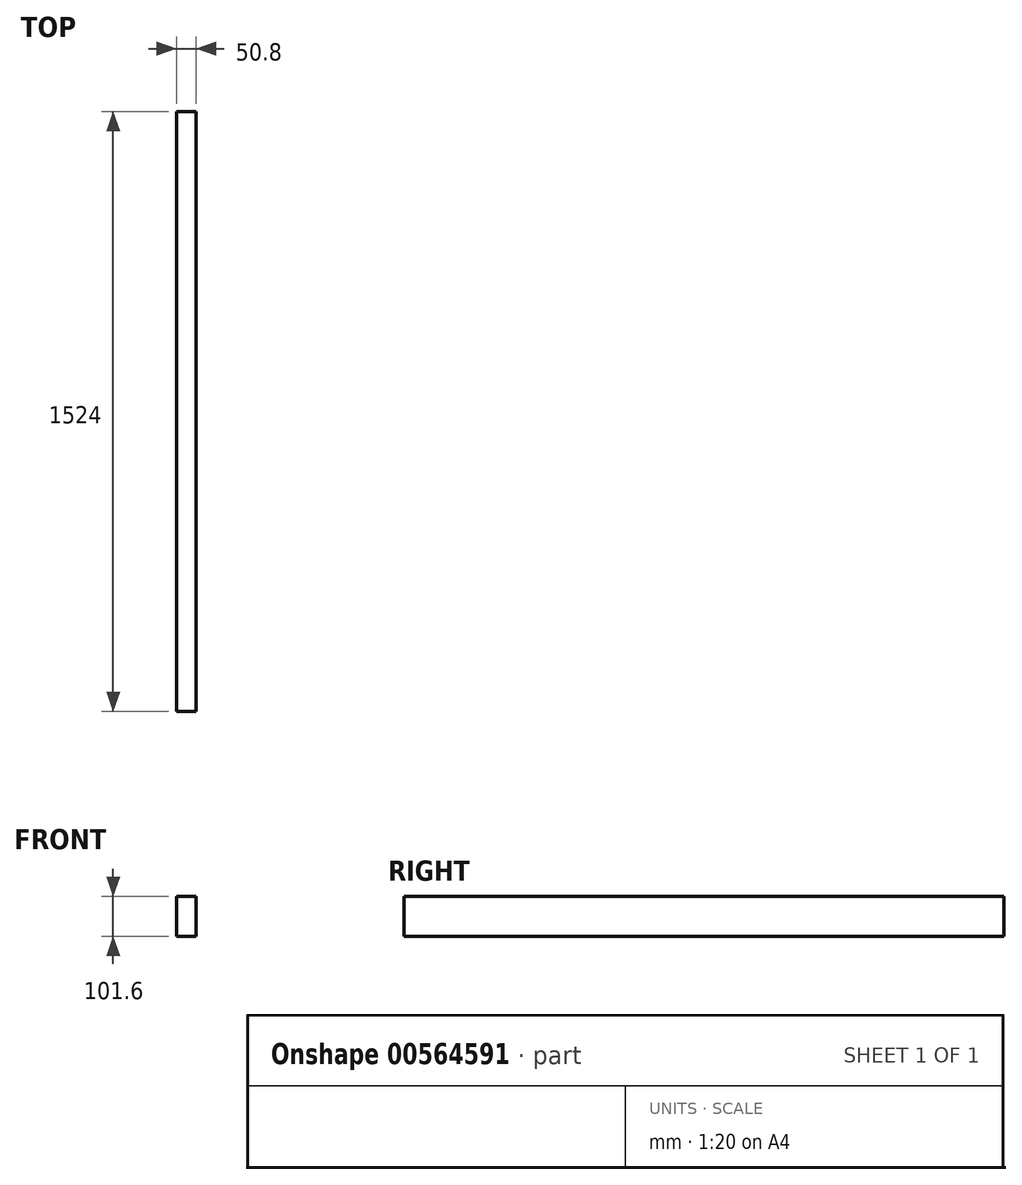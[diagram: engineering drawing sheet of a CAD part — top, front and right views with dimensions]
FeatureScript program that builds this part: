
annotation { "Feature Type Name" : "Feature", "Feature Type Description" : "" }
export const myFeature = defineFeature(function(context is Context, id is Id, definition is map)
    precondition{}
    {
        {
            var Q0;
            Q0=qCreatedBy(makeId("Front.planeOp"),FACE);
            var sketch = newSketch(context, id + "F0", { "sketchPlane" : qUnion([Q0])});
            skLineSegment(sketch, "E0.bottom", {"start": v(-21.64, 61.82) * mm, "end": v(29.16, 61.82) * mm});
            skLineSegment(sketch, "E0.top", {"start": v(-21.64, 163.42) * mm, "end": v(29.16, 163.42) * mm});
            skLineSegment(sketch, "E0.left", {"start": v(-21.64, 61.82) * mm, "end": v(-21.64, 163.42) * mm});
            skLineSegment(sketch, "E0.right", {"start": v(29.16, 61.82) * mm, "end": v(29.16, 163.42) * mm});
            skSolve(sketch);
        }
        {
            var Q0;
            Q0 = qSketchRegion(id + "F0", true);
            extrude(context, id + "F1", {"entities" : qUnion([Q0]), "depth" : 1524 * mm, "offsetDistance" : 25.4 * mm});
        }
    });
